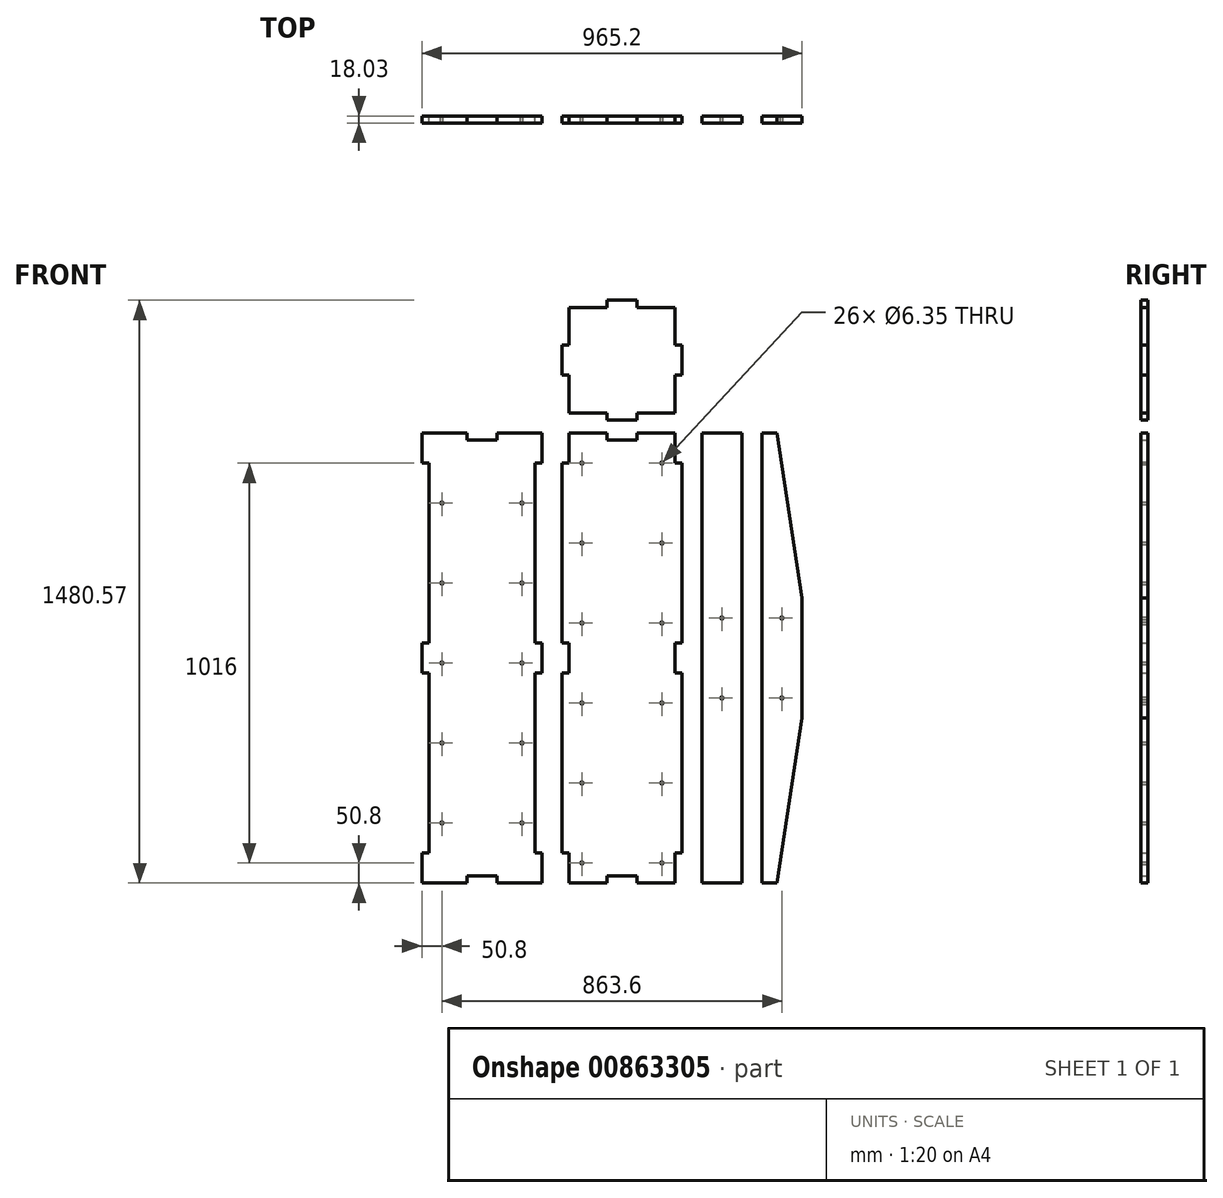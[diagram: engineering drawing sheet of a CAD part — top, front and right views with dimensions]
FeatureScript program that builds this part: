
annotation { "Feature Type Name" : "Feature", "Feature Type Description" : "" }
export const myFeature = defineFeature(function(context is Context, id is Id, definition is map)
    precondition{}
    {
        {
            var Q0;
            Q0=qCreatedBy(makeId("Front.planeOp"),FACE);
            var sketch = newSketch(context, id + "F0", { "sketchPlane" : qUnion([Q0])});
            skLineSegment(sketch, "E0.bottom", {"start": v(-152.4, 571.5) * mm, "end": v(152.4, 571.5) * mm});
            skLineSegment(sketch, "E0.top", {"start": v(-152.4, -571.5) * mm, "end": v(152.4, -571.5) * mm});
            skLineSegment(sketch, "E0.left", {"start": v(-152.4, 571.5) * mm, "end": v(-152.4, -571.5) * mm});
            skLineSegment(sketch, "E0.right", {"start": v(152.4, 571.5) * mm, "end": v(152.4, -571.5) * mm});
            skPoint(sketch, "E0.middle", {"position": v(0, 0) * mm});
            skLineSegment(sketch, "E1.bottom", {"start": v(203.2, 571.5) * mm, "end": v(304.8, 571.5) * mm});
            skLineSegment(sketch, "E1.top", {"start": v(203.2, -571.5) * mm, "end": v(304.8, -571.5) * mm});
            skLineSegment(sketch, "E1.left", {"start": v(203.2, 571.5) * mm, "end": v(203.2, -571.5) * mm});
            skLineSegment(sketch, "E1.right", {"start": v(304.8, 571.5) * mm, "end": v(304.8, -571.5) * mm});
            skPoint(sketch, "E1.middle", {"position": v(254, 0) * mm});
            skLineSegment(sketch, "E2.bottom", {"start": v(355.6, 571.5) * mm, "end": v(457.2, 571.5) * mm});
            skLineSegment(sketch, "E2.top", {"start": v(355.6, -571.5) * mm, "end": v(457.2, -571.5) * mm});
            skLineSegment(sketch, "E2.left", {"start": v(355.6, 571.5) * mm, "end": v(355.6, -571.5) * mm});
            skLineSegment(sketch, "E2.right", {"start": v(457.2, 571.5) * mm, "end": v(457.2, -571.5) * mm});
            skPoint(sketch, "E2.middle", {"position": v(406.4, 0) * mm});
            skLineSegment(sketch, "E3", {"start": v(457.2, 0) * mm, "end": v(355.6, 0) * mm, "construction": true});
            skLineSegment(sketch, "E4", {"start": v(457.2, 152.4) * mm, "end": v(393.7, 571.5) * mm});
            skLineSegment(sketch, "E5.MirrorCS", {"start": v(457.2, -152.4) * mm, "end": v(393.7, -571.5) * mm});
            skLineSegment(sketch, "E6.bottom", {"start": v(-152.4, 571.5) * mm, "end": v(-134.37, 571.5) * mm});
            skLineSegment(sketch, "E6.top", {"start": v(-152.4, 495.3) * mm, "end": v(-134.37, 495.3) * mm});
            skLineSegment(sketch, "E6.left", {"start": v(-152.4, 571.5) * mm, "end": v(-152.4, 495.3) * mm});
            skLineSegment(sketch, "E6.right", {"start": v(-134.37, 571.5) * mm, "end": v(-134.37, 495.3) * mm});
            skLineSegment(sketch, "E7", {"start": v(0, 0) * mm, "end": v(-152.4, 0) * mm, "construction": true});
            skLineSegment(sketch, "E8", {"start": v(0, 0) * mm, "end": v(0, 571.5) * mm, "construction": true});
            skLineSegment(sketch, "E9.bottom", {"start": v(-152.4, 0) * mm, "end": v(-134.37, 0) * mm});
            skLineSegment(sketch, "E9.top", {"start": v(-152.4, 38.1) * mm, "end": v(-134.37, 38.1) * mm});
            skLineSegment(sketch, "E9.left", {"start": v(-152.4, 0) * mm, "end": v(-152.4, 38.1) * mm});
            skLineSegment(sketch, "E9.right", {"start": v(-134.37, 0) * mm, "end": v(-134.37, 38.1) * mm});
            skLineSegment(sketch, "E10.MirrorCS", {"start": v(-152.4, -38.1) * mm, "end": v(-134.37, -38.1) * mm});
            skLineSegment(sketch, "E11.MirrorCS", {"start": v(-134.37, 0) * mm, "end": v(-134.37, -38.1) * mm});
            skLineSegment(sketch, "E12.MirrorCS", {"start": v(-152.4, 0) * mm, "end": v(-152.4, -38.1) * mm});
            skLineSegment(sketch, "E13.MirrorCS", {"start": v(-152.4, -495.3) * mm, "end": v(-134.37, -495.3) * mm});
            skLineSegment(sketch, "E14.MirrorCS", {"start": v(-152.4, -571.5) * mm, "end": v(-152.4, -495.3) * mm});
            skLineSegment(sketch, "E15.MirrorCS", {"start": v(-152.4, -571.5) * mm, "end": v(-134.37, -571.5) * mm});
            skLineSegment(sketch, "E16.MirrorCS", {"start": v(-134.37, -571.5) * mm, "end": v(-134.37, -495.3) * mm});
            skLineSegment(sketch, "E17.MirrorCS", {"start": v(152.4, 0) * mm, "end": v(134.37, 0) * mm});
            skLineSegment(sketch, "E18.MirrorCS", {"start": v(152.4, 495.3) * mm, "end": v(134.37, 495.3) * mm});
            skLineSegment(sketch, "E19.MirrorCS", {"start": v(152.4, 571.5) * mm, "end": v(134.37, 571.5) * mm});
            skLineSegment(sketch, "E20.MirrorCS", {"start": v(152.4, 38.1) * mm, "end": v(134.37, 38.1) * mm});
            skLineSegment(sketch, "E21.MirrorCS", {"start": v(152.4, -38.1) * mm, "end": v(134.37, -38.1) * mm});
            skLineSegment(sketch, "E22.MirrorCS", {"start": v(152.4, 0) * mm, "end": v(152.4, 38.1) * mm});
            skLineSegment(sketch, "E23.MirrorCS", {"start": v(152.4, 571.5) * mm, "end": v(152.4, 495.3) * mm});
            skLineSegment(sketch, "E24.MirrorCS", {"start": v(134.37, 571.5) * mm, "end": v(134.37, 495.3) * mm});
            skLineSegment(sketch, "E25.MirrorCS", {"start": v(134.37, 0) * mm, "end": v(134.37, -38.1) * mm});
            skLineSegment(sketch, "E26.MirrorCS", {"start": v(134.37, 0) * mm, "end": v(134.37, 38.1) * mm});
            skLineSegment(sketch, "E27.MirrorCS", {"start": v(152.4, 0) * mm, "end": v(152.4, -38.1) * mm});
            skLineSegment(sketch, "E28.MirrorCS", {"start": v(152.4, -495.3) * mm, "end": v(134.37, -495.3) * mm});
            skLineSegment(sketch, "E29.MirrorCS", {"start": v(152.4, -571.5) * mm, "end": v(134.37, -571.5) * mm});
            skLineSegment(sketch, "E30.MirrorCS", {"start": v(134.37, -571.5) * mm, "end": v(134.37, -495.3) * mm});
            skLineSegment(sketch, "E31.MirrorCS", {"start": v(152.4, -571.5) * mm, "end": v(152.4, -495.3) * mm});
            skLineSegment(sketch, "E32.bottom", {"start": v(-203.2, 571.5) * mm, "end": v(-508, 571.5) * mm});
            skLineSegment(sketch, "E32.top", {"start": v(-203.2, -571.5) * mm, "end": v(-508, -571.5) * mm});
            skLineSegment(sketch, "E32.left", {"start": v(-203.2, 571.5) * mm, "end": v(-203.2, -571.5) * mm});
            skLineSegment(sketch, "E32.right", {"start": v(-508, 571.5) * mm, "end": v(-508, -571.5) * mm});
            skPoint(sketch, "E32.middle", {"position": v(-355.6, 0) * mm});
            skLineSegment(sketch, "E33.bottom", {"start": v(-203.2, 495.3) * mm, "end": v(-221.23, 495.3) * mm});
            skLineSegment(sketch, "E33.top", {"start": v(-203.2, 38.1) * mm, "end": v(-221.23, 38.1) * mm});
            skLineSegment(sketch, "E33.left", {"start": v(-203.2, 495.3) * mm, "end": v(-203.2, 38.1) * mm});
            skLineSegment(sketch, "E33.right", {"start": v(-221.23, 495.3) * mm, "end": v(-221.23, 38.1) * mm});
            skLineSegment(sketch, "E34.bottom", {"start": v(-203.2, -495.3) * mm, "end": v(-221.23, -495.3) * mm});
            skLineSegment(sketch, "E34.top", {"start": v(-203.2, -38.1) * mm, "end": v(-221.23, -38.1) * mm});
            skLineSegment(sketch, "E34.left", {"start": v(-203.2, -495.3) * mm, "end": v(-203.2, -38.1) * mm});
            skLineSegment(sketch, "E34.right", {"start": v(-221.23, -495.3) * mm, "end": v(-221.23, -38.1) * mm});
            skLineSegment(sketch, "E35", {"start": v(-355.6, 0) * mm, "end": v(-355.6, 571.5) * mm, "construction": true});
            skLineSegment(sketch, "E36.MirrorCS", {"start": v(-508, 38.1) * mm, "end": v(-489.97, 38.1) * mm});
            skLineSegment(sketch, "E37.MirrorCS", {"start": v(-508, 495.3) * mm, "end": v(-489.97, 495.3) * mm});
            skLineSegment(sketch, "E38.MirrorCS", {"start": v(-508, 495.3) * mm, "end": v(-508, 38.1) * mm});
            skLineSegment(sketch, "E39.MirrorCS", {"start": v(-489.97, 495.3) * mm, "end": v(-489.97, 38.1) * mm});
            skLineSegment(sketch, "E40.MirrorCS", {"start": v(-508, -38.1) * mm, "end": v(-489.97, -38.1) * mm});
            skLineSegment(sketch, "E41.MirrorCS", {"start": v(-508, -495.3) * mm, "end": v(-489.97, -495.3) * mm});
            skLineSegment(sketch, "E42.MirrorCS", {"start": v(-508, -495.3) * mm, "end": v(-508, -38.1) * mm});
            skLineSegment(sketch, "E43.MirrorCS", {"start": v(-489.97, -495.3) * mm, "end": v(-489.97, -38.1) * mm});
            skCircle(sketch, "E44", {"center": v(406.4, 101.6) * mm, "radius": 3.18 * mm});
            skCircle(sketch, "E45.MirrorC", {"center": v(406.4, -101.6) * mm, "radius": 3.18 * mm});
            skCircle(sketch, "E46", {"center": v(254, 101.6) * mm, "radius": 3.18 * mm});
            skCircle(sketch, "E47.MirrorC", {"center": v(254, -101.6) * mm, "radius": 3.18 * mm});
            skLineSegment(sketch, "E48", {"start": v(0, -571.5) * mm, "end": v(0, -495.3) * mm, "construction": true});
            skCircle(sketch, "E49", {"center": v(-101.6, -520.7) * mm, "radius": 3.18 * mm});
            skCircle(sketch, "E50.MirrorC", {"center": v(101.6, -520.7) * mm, "radius": 3.18 * mm});
            skCircle(sketch, "E51", {"center": v(-457.2, -419.1) * mm, "radius": 3.18 * mm});
            skCircle(sketch, "E52.MirrorC", {"center": v(-254, -419.1) * mm, "radius": 3.18 * mm});
            skCircle(sketch, "E53.0.1.0", {"center": v(-101.6, -317.5) * mm, "radius": 3.18 * mm});
            skCircle(sketch, "E53.0.1.1", {"center": v(101.6, -317.5) * mm, "radius": 3.18 * mm});
            skCircle(sketch, "E53.0.1.2", {"center": v(-457.2, -215.9) * mm, "radius": 3.18 * mm});
            skCircle(sketch, "E53.0.1.3", {"center": v(-254, -215.9) * mm, "radius": 3.18 * mm});
            skCircle(sketch, "E53.0.2.0", {"center": v(-101.6, -114.3) * mm, "radius": 3.18 * mm});
            skCircle(sketch, "E53.0.2.1", {"center": v(101.6, -114.3) * mm, "radius": 3.18 * mm});
            skCircle(sketch, "E53.0.2.2", {"center": v(-457.2, -12.7) * mm, "radius": 3.18 * mm});
            skCircle(sketch, "E53.0.2.3", {"center": v(-254, -12.7) * mm, "radius": 3.18 * mm});
            skCircle(sketch, "E53.0.3.0", {"center": v(-101.6, 88.9) * mm, "radius": 3.18 * mm});
            skCircle(sketch, "E53.0.3.1", {"center": v(101.6, 88.9) * mm, "radius": 3.18 * mm});
            skCircle(sketch, "E53.0.3.2", {"center": v(-457.2, 190.5) * mm, "radius": 3.18 * mm});
            skCircle(sketch, "E53.0.3.3", {"center": v(-254, 190.5) * mm, "radius": 3.18 * mm});
            skCircle(sketch, "E53.0.4.0", {"center": v(-101.6, 292.1) * mm, "radius": 3.18 * mm});
            skCircle(sketch, "E53.0.4.1", {"center": v(101.6, 292.1) * mm, "radius": 3.18 * mm});
            skCircle(sketch, "E53.0.4.2", {"center": v(-457.2, 393.7) * mm, "radius": 3.18 * mm});
            skCircle(sketch, "E53.0.4.3", {"center": v(-254, 393.7) * mm, "radius": 3.18 * mm});
            skLineSegment(sketch, "E53.direction1", {"start": v(-101.6, -520.7) * mm, "end": v(-76.2, -520.7) * mm, "construction": true});
            skLineSegment(sketch, "E53.direction2", {"start": v(-101.6, -520.7) * mm, "end": v(-101.6, -317.5) * mm, "construction": true});
            skCircle(sketch, "E54.0.0.5", {"center": v(-101.6, 495.3) * mm, "radius": 3.18 * mm});
            skCircle(sketch, "E54.2.0.5", {"center": v(101.6, 495.3) * mm, "radius": 3.18 * mm});
            skLineSegment(sketch, "E55.bottom", {"start": v(-393.7, 571.5) * mm, "end": v(-317.5, 571.5) * mm});
            skLineSegment(sketch, "E55.top", {"start": v(-393.7, 553.47) * mm, "end": v(-317.5, 553.47) * mm});
            skLineSegment(sketch, "E55.left", {"start": v(-393.7, 571.5) * mm, "end": v(-393.7, 553.47) * mm});
            skLineSegment(sketch, "E55.right", {"start": v(-317.5, 571.5) * mm, "end": v(-317.5, 553.47) * mm});
            skPoint(sketch, "E55.middle", {"position": v(-355.6, 562.48) * mm});
            skLineSegment(sketch, "E56.bottom", {"start": v(-38.1, 571.5) * mm, "end": v(38.1, 571.5) * mm});
            skLineSegment(sketch, "E56.top", {"start": v(-38.1, 553.47) * mm, "end": v(38.1, 553.47) * mm});
            skLineSegment(sketch, "E56.left", {"start": v(-38.1, 571.5) * mm, "end": v(-38.1, 553.47) * mm});
            skLineSegment(sketch, "E56.right", {"start": v(38.1, 571.5) * mm, "end": v(38.1, 553.47) * mm});
            skPoint(sketch, "E56.middle", {"position": v(0, 562.48) * mm});
            skLineSegment(sketch, "E57.bottom", {"start": v(-134.37, 622.3) * mm, "end": v(134.37, 622.3) * mm});
            skLineSegment(sketch, "E57.top", {"start": v(-134.37, 891.03) * mm, "end": v(134.37, 891.03) * mm});
            skLineSegment(sketch, "E57.left", {"start": v(-134.37, 622.3) * mm, "end": v(-134.37, 891.03) * mm});
            skLineSegment(sketch, "E57.right", {"start": v(134.37, 622.3) * mm, "end": v(134.37, 891.03) * mm});
            skPoint(sketch, "E57.middle", {"position": v(0, 756.67) * mm});
            skLineSegment(sketch, "E58.bottom", {"start": v(-38.1, 622.3) * mm, "end": v(38.1, 622.3) * mm});
            skLineSegment(sketch, "E58.top", {"start": v(-38.1, 604.27) * mm, "end": v(38.1, 604.27) * mm});
            skLineSegment(sketch, "E58.left", {"start": v(-38.1, 622.3) * mm, "end": v(-38.1, 604.27) * mm});
            skLineSegment(sketch, "E58.right", {"start": v(38.1, 622.3) * mm, "end": v(38.1, 604.27) * mm});
            skPoint(sketch, "E58.middle", {"position": v(0, 613.28) * mm});
            skPoint(sketch, "E58.middle.positionSnap0", {"position": v(0, 622.3) * mm});
            skPoint(sketch, "E58.centerSnap0", {"position": v(0, 622.3) * mm});
            skPoint(sketch, "E59.1.0", {"position": v(134.37, 756.67) * mm});
            skPoint(sketch, "E59.1.1", {"position": v(143.38, 756.67) * mm});
            skLineSegment(sketch, "E59.1.2", {"start": v(152.4, 718.57) * mm, "end": v(152.4, 794.77) * mm});
            skLineSegment(sketch, "E59.1.3", {"start": v(134.37, 718.57) * mm, "end": v(134.37, 794.77) * mm});
            skLineSegment(sketch, "E59.1.4", {"start": v(134.37, 794.77) * mm, "end": v(152.4, 794.77) * mm});
            skLineSegment(sketch, "E59.1.5", {"start": v(134.37, 718.57) * mm, "end": v(152.4, 718.57) * mm});
            skPoint(sketch, "E59.1.6", {"position": v(134.37, 756.67) * mm});
            skPoint(sketch, "E59.2.0", {"position": v(0, 891.03) * mm});
            skPoint(sketch, "E59.2.1", {"position": v(0, 900.05) * mm});
            skLineSegment(sketch, "E59.2.2", {"start": v(38.1, 909.07) * mm, "end": v(-38.1, 909.07) * mm});
            skLineSegment(sketch, "E59.2.3", {"start": v(38.1, 891.03) * mm, "end": v(-38.1, 891.03) * mm});
            skLineSegment(sketch, "E59.2.4", {"start": v(-38.1, 891.03) * mm, "end": v(-38.1, 909.07) * mm});
            skLineSegment(sketch, "E59.2.5", {"start": v(38.1, 891.03) * mm, "end": v(38.1, 909.07) * mm});
            skPoint(sketch, "E59.2.6", {"position": v(0, 891.03) * mm});
            skPoint(sketch, "E59.3.0", {"position": v(-134.37, 756.67) * mm});
            skPoint(sketch, "E59.3.1", {"position": v(-143.38, 756.67) * mm});
            skLineSegment(sketch, "E59.3.2", {"start": v(-152.4, 794.77) * mm, "end": v(-152.4, 718.57) * mm});
            skLineSegment(sketch, "E59.3.3", {"start": v(-134.37, 794.77) * mm, "end": v(-134.37, 718.57) * mm});
            skLineSegment(sketch, "E59.3.4", {"start": v(-134.37, 718.57) * mm, "end": v(-152.4, 718.57) * mm});
            skLineSegment(sketch, "E59.3.5", {"start": v(-134.37, 794.77) * mm, "end": v(-152.4, 794.77) * mm});
            skPoint(sketch, "E59.3.6", {"position": v(-134.37, 756.67) * mm});
            skPoint(sketch, "E60.MirrorP", {"position": v(0, -562.48) * mm});
            skLineSegment(sketch, "E61.MirrorCS", {"start": v(-38.1, -553.47) * mm, "end": v(38.1, -553.47) * mm});
            skLineSegment(sketch, "E62.MirrorCS", {"start": v(-38.1, -571.5) * mm, "end": v(38.1, -571.5) * mm});
            skLineSegment(sketch, "E63.MirrorCS", {"start": v(-38.1, -571.5) * mm, "end": v(-38.1, -553.47) * mm});
            skLineSegment(sketch, "E64.MirrorCS", {"start": v(38.1, -571.5) * mm, "end": v(38.1, -553.47) * mm});
            skPoint(sketch, "E65.MirrorP", {"position": v(-355.6, -562.48) * mm});
            skLineSegment(sketch, "E66.MirrorCS", {"start": v(-393.7, -571.5) * mm, "end": v(-317.5, -571.5) * mm});
            skLineSegment(sketch, "E67.MirrorCS", {"start": v(-393.7, -553.47) * mm, "end": v(-317.5, -553.47) * mm});
            skLineSegment(sketch, "E68.MirrorCS", {"start": v(-317.5, -571.5) * mm, "end": v(-317.5, -553.47) * mm});
            skLineSegment(sketch, "E69.MirrorCS", {"start": v(-393.7, -571.5) * mm, "end": v(-393.7, -553.47) * mm});
            skSolve(sketch);
        }
        {
            var Q0;
            {var subQ5=sQuery(id+"F0.wireOp",EDGE,"E33.bottom");Q0=makeQuery(id+"F0.imprint","IMPRINT",FACE,{"disambiguationData":[TD([[makeQuery(id+"F0.imprint","IMPRINT",EDGE,{"derivedFrom":subQ5}),-1.0]])]});}
            var Q1;
            {var subQ18=sQuery(id+"F0.wireOp",EDGE,"E6.top");Q1=makeQuery(id+"F0.imprint","IMPRINT",FACE,{"disambiguationData":[TD([[makeQuery(id+"F0.imprint","IMPRINT",EDGE,{"derivedFrom":subQ18}),-1.0]])]});}
            var Q2;
            Q2=makeQuery(id+"F0.imprint","IMPRINT",FACE,{"disambiguationData":[TD([[makeQuery(id+"F0.imprint","IMPRINT",EDGE,{"derivedFrom":sQuery(id+"F0.wireOp",EDGE,"E1.bottom")}),-1.0]])]});
            var Q3;
            {var subQ3=sQuery(id+"F0.wireOp",EDGE,"E2.left");Q3=makeQuery(id+"F0.imprint","IMPRINT",FACE,{"disambiguationData":[TD([[makeQuery(id+"F0.imprint","IMPRINT",EDGE,{"derivedFrom":subQ3}),1.0]])]});}
            var Q4;
            {var subQ1=sQuery(id+"F0.wireOp",EDGE,"E57.bottom");var subQ4=sQuery(id+"F0.wireOp",EDGE,"E57.left");var subQ9=makeQuery(id+"F0.imprint","INTERSECT",VERTEX,{"derivedFrom":[subQ1,subQ4]});Q4=makeQuery(id+"F0.imprint","IMPRINT",FACE,{"disambiguationData":[TD([[makeQuery(id+"F0.imprint","IMPRINT",EDGE,{"disambiguationData":[TD([[subQ9,-1.0]])],"derivedFrom":subQ1}),1.0]])]});}
            var Q5;
            Q5=makeQuery(id+"F0.imprint","IMPRINT",FACE,{"disambiguationData":[TD([[makeQuery(id+"F0.imprint","IMPRINT",EDGE,{"derivedFrom":sQuery(id+"F0.wireOp",EDGE,"E59.2.2")}),1.0]])]});
            var Q6;
            Q6=makeQuery(id+"F0.imprint","IMPRINT",FACE,{"disambiguationData":[TD([[makeQuery(id+"F0.imprint","IMPRINT",EDGE,{"derivedFrom":sQuery(id+"F0.wireOp",EDGE,"E59.3.2")}),1.0]])]});
            var Q7;
            Q7=makeQuery(id+"F0.imprint","IMPRINT",FACE,{"disambiguationData":[TD([[makeQuery(id+"F0.imprint","IMPRINT",EDGE,{"derivedFrom":sQuery(id+"F0.wireOp",EDGE,"E58.top")}),1.0]])]});
            var Q8;
            Q8=makeQuery(id+"F0.imprint","IMPRINT",FACE,{"disambiguationData":[TD([[makeQuery(id+"F0.imprint","IMPRINT",EDGE,{"derivedFrom":sQuery(id+"F0.wireOp",EDGE,"E59.1.2")}),1.0]])]});
            extrude(context, id + "F1", {"entities" : qUnion([Q0, Q1, Q2, Q3, Q4, Q5, Q6, Q7, Q8]), "depth" : 18.03 * mm, "offsetDistance" : 25.4 * mm});
        }
    });
